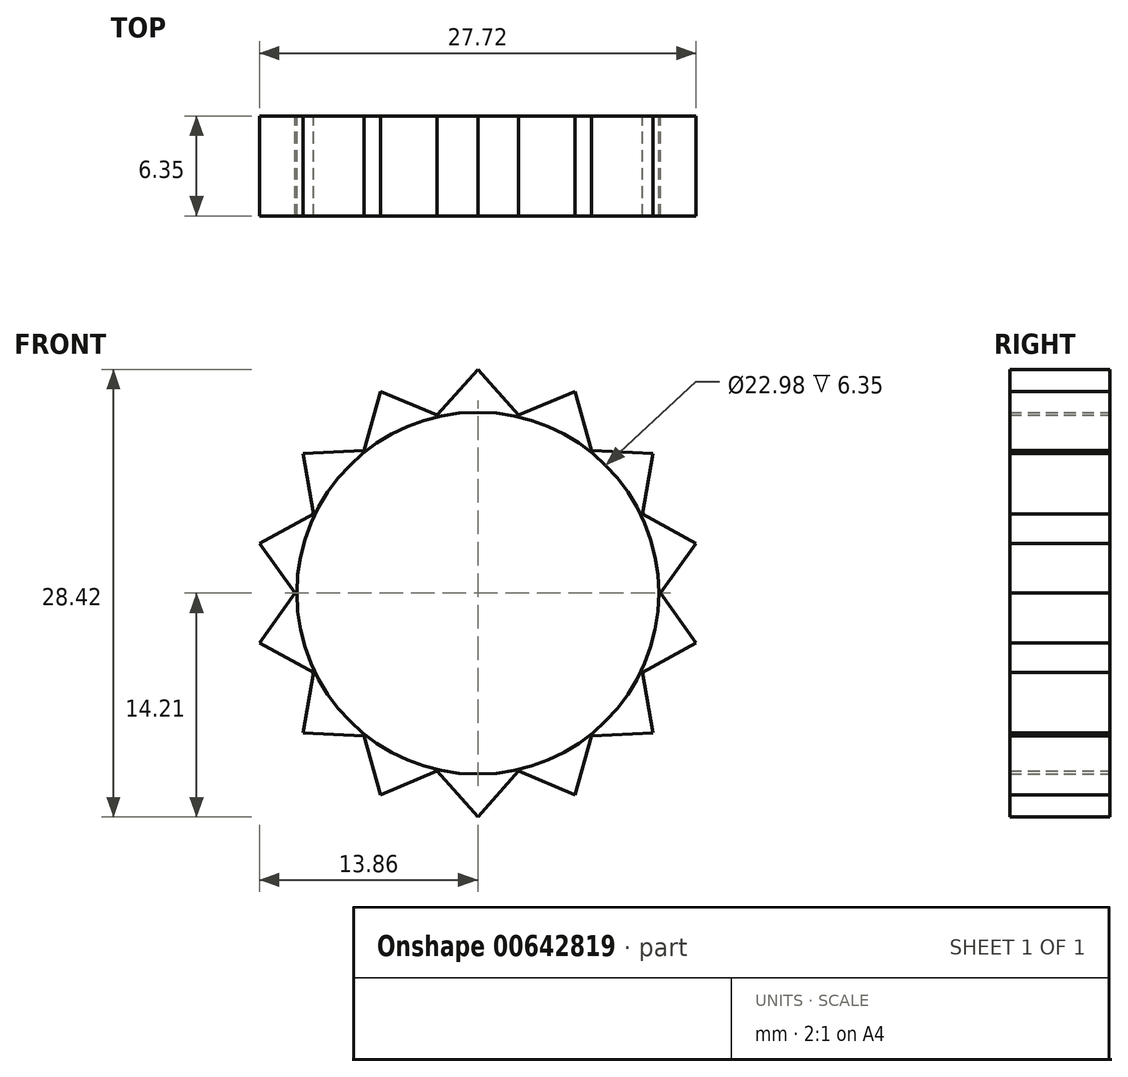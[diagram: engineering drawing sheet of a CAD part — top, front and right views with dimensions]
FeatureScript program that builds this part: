
annotation { "Feature Type Name" : "Feature", "Feature Type Description" : "" }
export const myFeature = defineFeature(function(context is Context, id is Id, definition is map)
    precondition{}
    {
        {
            var Q0;
            Q0=qCreatedBy(makeId("Front.planeOp"),FACE);
            var sketch = newSketch(context, id + "F0", { "sketchPlane" : qUnion([Q0])});
            skCircle(sketch, "E0", {"center": v(0, 0) * mm, "radius": 11.5 * mm});
            skLineSegment(sketch, "E1", {"start": v(0, 11.5) * mm, "end": v(0, 14.21) * mm, "construction": true});
            skLineSegment(sketch, "E2", {"start": v(0, 14.21) * mm, "end": v(2.7, 11.17) * mm});
            skLineSegment(sketch, "E3", {"start": v(0, 14.21) * mm, "end": v(-2.7, 11.17) * mm});
            skLineSegment(sketch, "E4.1.0", {"start": v(-6.17, 12.8) * mm, "end": v(-2.42, 11.23) * mm});
            skLineSegment(sketch, "E4.1.1", {"start": v(-6.17, 12.8) * mm, "end": v(-7.28, 8.9) * mm});
            skLineSegment(sketch, "E4.2.0", {"start": v(-11.11, 8.86) * mm, "end": v(-7.05, 9.07) * mm});
            skLineSegment(sketch, "E4.2.1", {"start": v(-11.11, 8.86) * mm, "end": v(-10.41, 4.86) * mm});
            skLineSegment(sketch, "E4.3.0", {"start": v(-13.86, 3.16) * mm, "end": v(-10.3, 5.11) * mm});
            skLineSegment(sketch, "E4.3.1", {"start": v(-13.86, 3.16) * mm, "end": v(-11.5, -0.14) * mm});
            skLineSegment(sketch, "E4.4.0", {"start": v(-13.86, -3.16) * mm, "end": v(-11.5, 0.14) * mm});
            skLineSegment(sketch, "E4.4.1", {"start": v(-13.86, -3.16) * mm, "end": v(-10.3, -5.11) * mm});
            skLineSegment(sketch, "E4.5.0", {"start": v(-11.11, -8.86) * mm, "end": v(-10.41, -4.86) * mm});
            skLineSegment(sketch, "E4.5.1", {"start": v(-11.11, -8.86) * mm, "end": v(-7.05, -9.07) * mm});
            skLineSegment(sketch, "E4.6.0", {"start": v(-6.17, -12.8) * mm, "end": v(-7.28, -8.9) * mm});
            skLineSegment(sketch, "E4.6.1", {"start": v(-6.17, -12.8) * mm, "end": v(-2.42, -11.23) * mm});
            skLineSegment(sketch, "E4.7.0", {"start": v(0, -14.21) * mm, "end": v(-2.7, -11.17) * mm});
            skLineSegment(sketch, "E4.7.1", {"start": v(0, -14.21) * mm, "end": v(2.7, -11.17) * mm});
            skLineSegment(sketch, "E4.8.0", {"start": v(6.17, -12.8) * mm, "end": v(2.42, -11.23) * mm});
            skLineSegment(sketch, "E4.8.1", {"start": v(6.17, -12.8) * mm, "end": v(7.28, -8.9) * mm});
            skLineSegment(sketch, "E4.9.0", {"start": v(11.11, -8.86) * mm, "end": v(7.05, -9.07) * mm});
            skLineSegment(sketch, "E4.9.1", {"start": v(11.11, -8.86) * mm, "end": v(10.41, -4.86) * mm});
            skLineSegment(sketch, "E4.10.0", {"start": v(13.86, -3.16) * mm, "end": v(10.3, -5.11) * mm});
            skLineSegment(sketch, "E4.10.1", {"start": v(13.86, -3.16) * mm, "end": v(11.5, 0.14) * mm});
            skLineSegment(sketch, "E4.11.0", {"start": v(13.86, 3.16) * mm, "end": v(11.5, -0.14) * mm});
            skLineSegment(sketch, "E4.11.1", {"start": v(13.86, 3.16) * mm, "end": v(10.3, 5.11) * mm});
            skLineSegment(sketch, "E4.12.0", {"start": v(11.11, 8.86) * mm, "end": v(10.41, 4.86) * mm});
            skLineSegment(sketch, "E4.12.1", {"start": v(11.11, 8.86) * mm, "end": v(7.05, 9.07) * mm});
            skLineSegment(sketch, "E4.13.0", {"start": v(6.17, 12.8) * mm, "end": v(7.28, 8.9) * mm});
            skLineSegment(sketch, "E4.13.1", {"start": v(6.17, 12.8) * mm, "end": v(2.42, 11.23) * mm});
            skSolve(sketch);
        }
        {
            var Q0;
            Q0 = qSketchRegion(id + "F0", true);
            extrude(context, id + "F1", {"entities" : qUnion([Q0]), "depth" : 6.35 * mm, "offsetDistance" : 25.4 * mm});
        }
    });
